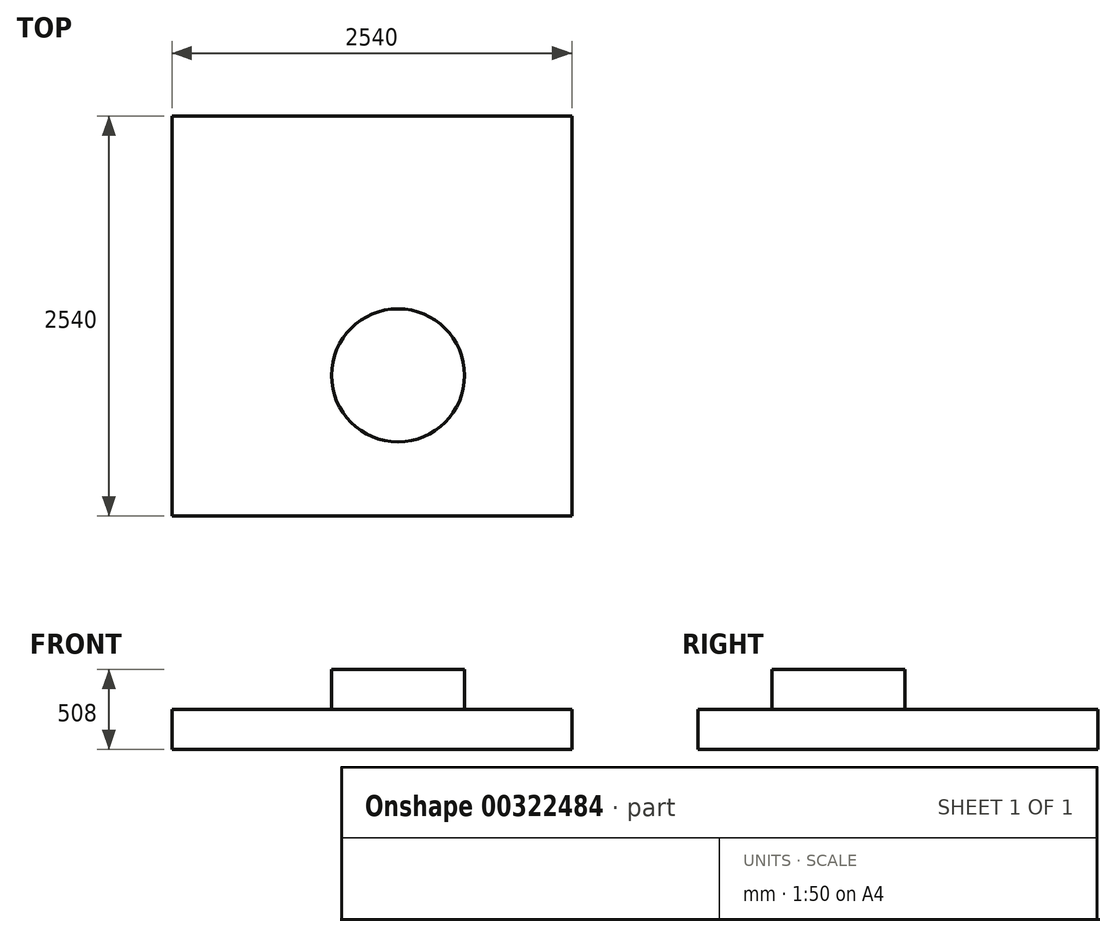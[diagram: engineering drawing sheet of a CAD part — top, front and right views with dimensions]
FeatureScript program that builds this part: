
annotation { "Feature Type Name" : "Feature", "Feature Type Description" : "" }
export const myFeature = defineFeature(function(context is Context, id is Id, definition is map)
    precondition{}
    {
        {
            var Q0;
            Q0=qCreatedBy(makeId("Top.planeOp"),FACE);
            var sketch = newSketch(context, id + "F0", { "sketchPlane" : qUnion([Q0])});
            skLineSegment(sketch, "E0.bottom", {"start": v(0, 0) * mm, "end": v(2540, 0) * mm});
            skLineSegment(sketch, "E0.top", {"start": v(0, 2540) * mm, "end": v(2540, 2540) * mm});
            skLineSegment(sketch, "E0.left", {"start": v(0, 0) * mm, "end": v(0, 2540) * mm});
            skLineSegment(sketch, "E0.right", {"start": v(2540, 0) * mm, "end": v(2540, 2540) * mm});
            skSolve(sketch);
        }
        {
            var Q0;
            Q0 = qSketchRegion(id + "F0", true);
            extrude(context, id + "F1", {"entities" : qUnion([Q0]), "depth" : 508 * mm});
        }
        {
            var Q0;
            Q0=makeQuery(id+"F1.opExtrude","CAP_FACE",FACE,{"disambiguationData":[OSD([sQuery(id+"F0.wireOp",EDGE,"E0.bottom"),sQuery(id+"F0.wireOp",EDGE,"E0.top"),sQuery(id+"F0.wireOp",EDGE,"E0.left"),sQuery(id+"F0.wireOp",EDGE,"E0.right")])],"isStart":false});
            var sketch = newSketch(context, id + "F2", { "sketchPlane" : qUnion([Q0])});
            skCircle(sketch, "E1", {"center": v(1436.32, 892.73) * mm, "radius": 422.57 * mm});
            skSolve(sketch);
        }
        {
            var Q0;
            Q0=makeQuery(id+"F2.imprint","IMPRINT",FACE,{"disambiguationData":[TD([[makeQuery(id+"F2.imprint","IMPRINT",EDGE,{"derivedFrom":sQuery(id+"F2.wireOp",EDGE,"E1")}),-1.0]])]});
            extrude(context, id + "F3", {"entities" : qUnion([Q0]), "operationType" : NewBodyOperationType.REMOVE, "oppositeDirection" : true, "depth" : 254 * mm});
        }
    });
